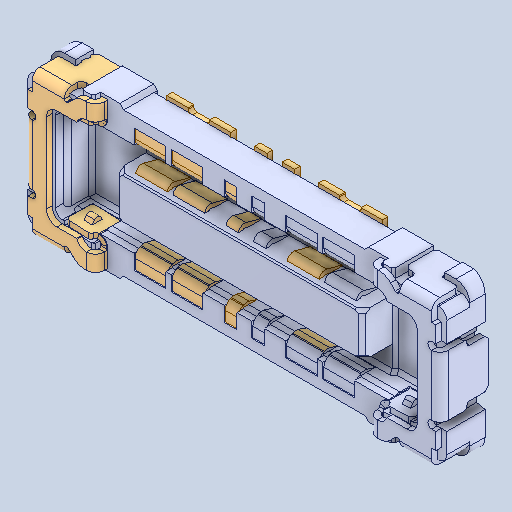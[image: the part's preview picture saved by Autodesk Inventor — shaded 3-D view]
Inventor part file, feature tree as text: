
AUTODESK INVENTOR PART (.ipt)
format: ipt  version: 2025 (Build 290162000, 162)  size: 939,008 bytes
history: native  units: mm
features: other x18, mirror x17
ambient origin geometry x8: Origin, YZ Plane, XZ Plane, XY Plane, X Axis, Y Axis, Z Axis, Center Point
bodies: Solid1 (feature_tree), Solid2 (feature_tree), Solid3 (feature_tree), Solid4 (feature_tree), Solid5 (feature_tree), Solid6 (feature_tree), Solid7 (feature_tree), Solid8 (feature_tree), Solid9 (feature_tree), Solid10 (feature_tree), Solid11 (feature_tree), Solid12 (feature_tree), Solid13 (feature_tree), Solid14 (feature_tree), Solid15 (feature_tree), Solid16 (feature_tree), Solid17 (feature_tree), Solid18 (feature_tree), Solid19 (feature_tree), Solid20 (feature_tree), Solid21 (feature_tree), Solid22 (feature_tree), Solid23 (feature_tree), Solid24 (feature_tree), Solid25 (feature_tree), Solid26 (feature_tree), Solid27 (feature_tree), Solid28 (feature_tree), Solid29 (feature_tree), Solid30 (feature_tree), Solid31 (feature_tree), Solid32 (feature_tree), Solid33 (feature_tree), Solid34 (feature_tree), Solid35 (feature_tree)
feature tree (35):
  mirror  "Mirror5[4]"
  mirror  "Mirror5[2]"
  other  "Boss-Extrude15"
  mirror  "Mirror5[5]"
  other  "Boss-Extrude11[4]"
  mirror  "Mirror5[6]"
  mirror  "Mirror5[3]"
  other  "Cut-Extrude9[2]"
  mirror  "Mirror5[9]"
  other  "Boss-Extrude14[1]"
  mirror  "Mirror5[10]"
  other  "Boss-Extrude12[1]"
  mirror  "Mirror5[7]"
  mirror  "Mirror5[11]"
  mirror  "Mirror4[4]"
  other  "Boss-Extrude13[2]"
  mirror  "Mirror5[1]"
  mirror  "Mirror2"
  other  "Boss-Extrude12[2]"
  mirror  "Mirror4[1]"
  other  "Boss-Extrude10[2]"
  other  "Boss-Extrude9[2]"
  other  "Boss-Extrude14[2]"
  other  "Boss-Extrude9[1]"
  other  "Cut-Extrude9[1]"
  other  "Boss-Extrude10[3]"
  other  "Boss-Extrude13[1]"
  other  "Boss-Extrude11[3]"
  other  "Cut-Extrude10"
  mirror  "Mirror5[12]"
  mirror  "Mirror4[2]"
  mirror  "Mirror4[3]"
  other  "LPattern1[1]"
  mirror  "Mirror5[8]"
  other  "LPattern1[3]"
